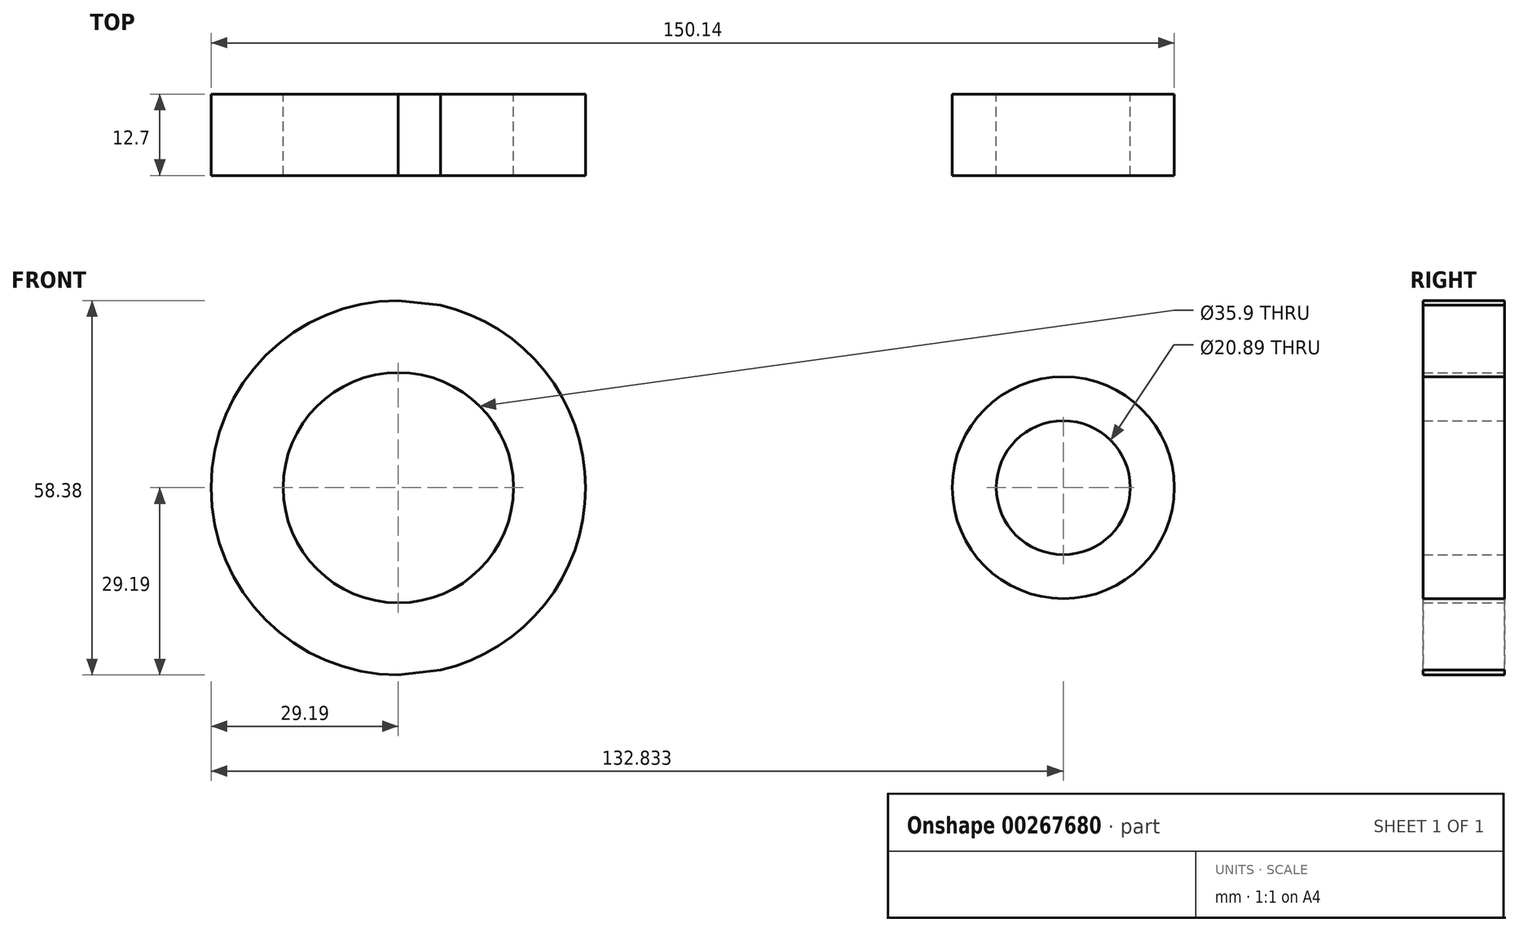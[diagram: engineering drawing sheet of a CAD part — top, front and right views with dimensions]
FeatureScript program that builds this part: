
annotation { "Feature Type Name" : "Feature", "Feature Type Description" : "" }
export const myFeature = defineFeature(function(context is Context, id is Id, definition is map)
    precondition{}
    {
        {
            var Q0;
            Q0=qCreatedBy(makeId("Front.planeOp"),FACE);
            var sketch = newSketch(context, id + "F0", { "sketchPlane" : qUnion([Q0])});
            skPoint(sketch, "E0.center.orphan", {"position": v(0, 37.4) * mm});
            skCircle(sketch, "E1", {"center": v(0, 0) * mm, "radius": 29.19 * mm});
            skCircle(sketch, "E2", {"center": v(103.64, 0) * mm, "radius": 17.3 * mm});
            skLineSegment(sketch, "E3", {"start": v(0, 29.19) * mm, "end": v(105.6, 17.2) * mm});
            skLineSegment(sketch, "E4", {"start": v(0, -29.19) * mm, "end": v(105.6, -17.2) * mm});
            skCircle(sketch, "E5", {"center": v(0, 0) * mm, "radius": 17.95 * mm});
            skCircle(sketch, "E6", {"center": v(103.64, 0) * mm, "radius": 10.45 * mm});
            skSolve(sketch);
        }
        {
            var Q0;
            {var subQ0=sQuery(id+"F0.wireOp",EDGE,"E3");var subQ1=sQuery(id+"F0.wireOp",EDGE,"E1");var subQ2=makeQuery(id+"F0.imprint","INTERSECT",VERTEX,{"disambiguationData":[OD(0.0)],"derivedFrom":[subQ1,subQ0]});Q0=makeQuery(id+"F0.imprint","IMPRINT",FACE,{"disambiguationData":[TD([[makeQuery(id+"F0.imprint","IMPRINT",EDGE,{"disambiguationData":[TD([[subQ2,1.0]])],"derivedFrom":subQ1}),1.0]])]});}
            var Q1;
            {var subQ0=sQuery(id+"F0.wireOp",EDGE,"E4");var subQ1=sQuery(id+"F0.wireOp",EDGE,"E1");var subQ2=makeQuery(id+"F0.imprint","INTERSECT",VERTEX,{"disambiguationData":[OD(0.0)],"derivedFrom":[subQ1,subQ0]});Q1=makeQuery(id+"F0.imprint","IMPRINT",FACE,{"disambiguationData":[TD([[makeQuery(id+"F0.imprint","IMPRINT",EDGE,{"disambiguationData":[TD([[subQ2,-1.0]])],"derivedFrom":subQ1}),1.0]])]});}
            var Q2;
            {var subQ0=sQuery(id+"F0.wireOp",EDGE,"E3");var subQ1=sQuery(id+"F0.wireOp",EDGE,"E1");var subQ2=makeQuery(id+"F0.imprint","INTERSECT",VERTEX,{"disambiguationData":[OD(1.0)],"derivedFrom":[subQ1,subQ0]});Q2=makeQuery(id+"F0.imprint","IMPRINT",FACE,{"disambiguationData":[TD([[makeQuery(id+"F0.imprint","IMPRINT",EDGE,{"disambiguationData":[TD([[subQ2,1.0]])],"derivedFrom":subQ1}),-1.0]])]});}
            var Q3;
            Q3=makeQuery(id+"F0.imprint","IMPRINT",FACE,{"disambiguationData":[TD([[makeQuery(id+"F0.imprint","IMPRINT",EDGE,{"derivedFrom":sQuery(id+"F0.wireOp",EDGE,"E6")}),-1.0]])]});
            var Q4;
            Q4=makeQuery(id+"F0.imprint","IMPRINT",FACE,{"disambiguationData":[TD([[makeQuery(id+"F0.imprint","IMPRINT",EDGE,{"derivedFrom":sQuery(id+"F0.wireOp",EDGE,"E5")}),-1.0]])]});
            extrude(context, id + "F1", {"entities" : qUnion([Q0, Q1, Q2, Q3, Q4]), "depth" : 12.7 * mm});
        }
    });
